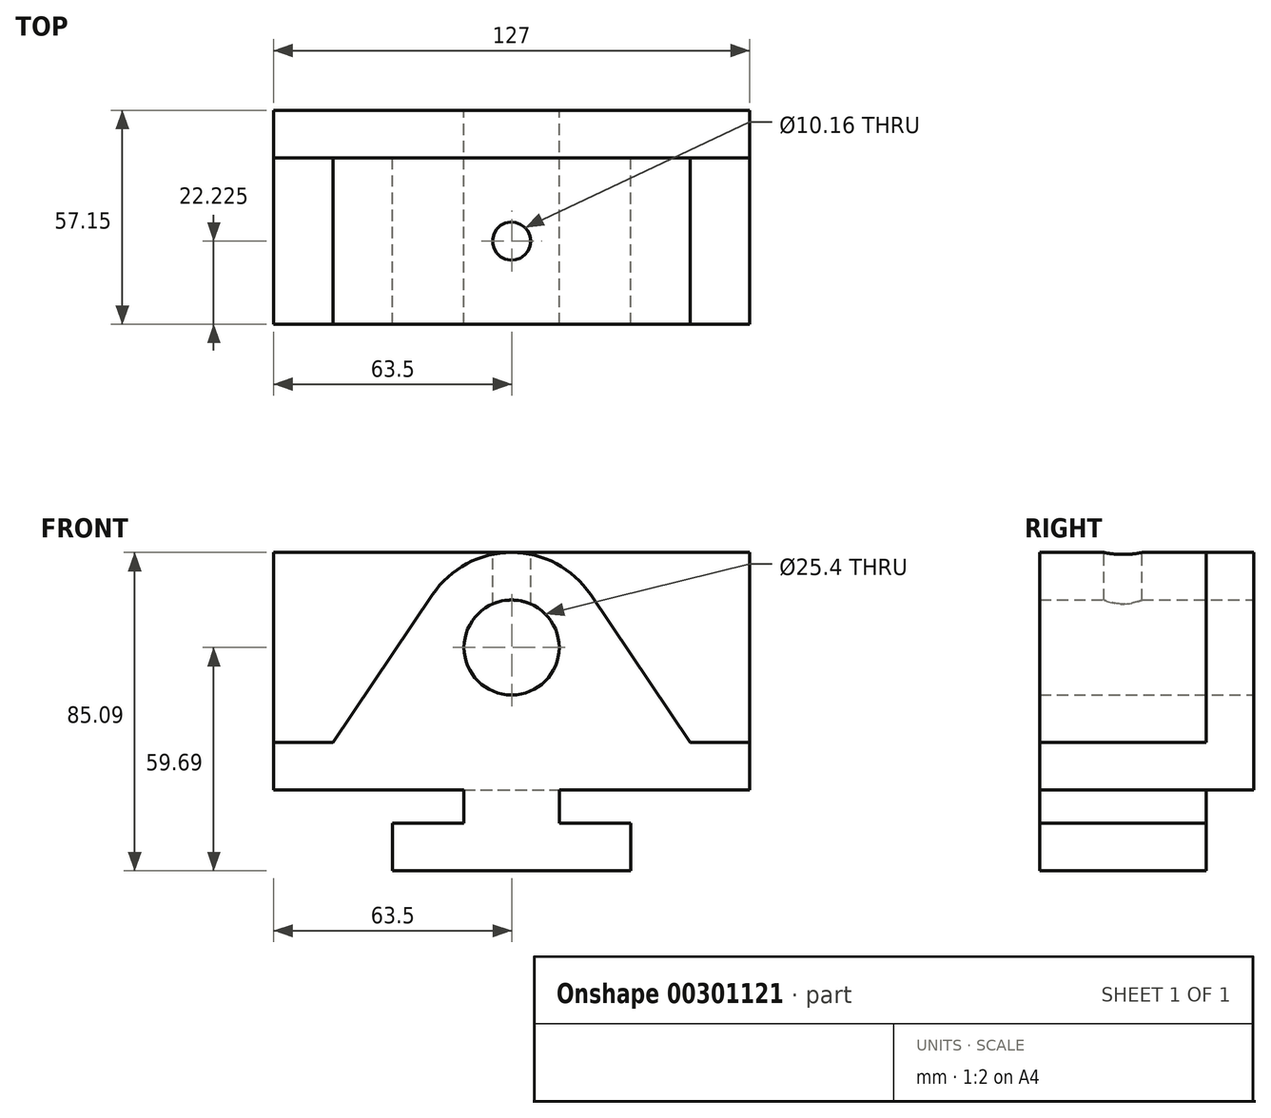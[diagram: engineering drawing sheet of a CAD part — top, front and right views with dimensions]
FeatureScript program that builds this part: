
annotation { "Feature Type Name" : "Feature", "Feature Type Description" : "" }
export const myFeature = defineFeature(function(context is Context, id is Id, definition is map)
    precondition{}
    {
        {
            var Q0;
            Q0=qCreatedBy(makeId("Front.planeOp"),FACE);
            var sketch = newSketch(context, id + "F0", { "sketchPlane" : qUnion([Q0])});
            skLineSegment(sketch, "E0", {"start": v(0, 0) * mm, "end": v(0, 12.7) * mm});
            skLineSegment(sketch, "E1", {"start": v(0, 12.7) * mm, "end": v(15.87, 12.7) * mm});
            skLineSegment(sketch, "E2", {"start": v(15.87, 12.7) * mm, "end": v(42.4, 52.25) * mm});
            skArc(sketch, "E3", {"start": v(84.6, 52.25) * mm, "mid": v(63.5, 63.5) * mm, "end": v(42.4, 52.25) * mm});
            skLineSegment(sketch, "E4", {"start": v(84.6, 52.25) * mm, "end": v(111.12, 12.7) * mm});
            skLineSegment(sketch, "E5", {"start": v(111.12, 12.7) * mm, "end": v(127, 12.7) * mm});
            skLineSegment(sketch, "E6", {"start": v(127, 12.7) * mm, "end": v(127, 0) * mm});
            skLineSegment(sketch, "E7", {"start": v(127, 0) * mm, "end": v(76.2, 0) * mm});
            skLineSegment(sketch, "E8", {"start": v(76.2, 0) * mm, "end": v(76.2, -8.89) * mm});
            skLineSegment(sketch, "E9", {"start": v(76.2, -8.89) * mm, "end": v(95.25, -8.89) * mm});
            skLineSegment(sketch, "E10", {"start": v(95.25, -8.89) * mm, "end": v(95.25, -21.6) * mm});
            skLineSegment(sketch, "E11", {"start": v(95.25, -21.6) * mm, "end": v(31.75, -21.6) * mm});
            skLineSegment(sketch, "E12", {"start": v(31.75, -21.6) * mm, "end": v(31.75, -8.89) * mm});
            skLineSegment(sketch, "E13", {"start": v(31.75, -8.89) * mm, "end": v(50.8, -8.89) * mm});
            skLineSegment(sketch, "E14", {"start": v(50.8, -8.89) * mm, "end": v(50.8, 0) * mm});
            skLineSegment(sketch, "E15", {"start": v(50.8, 0) * mm, "end": v(0, 0) * mm});
            skCircle(sketch, "E16", {"center": v(63.5, 38.1) * mm, "radius": 12.7 * mm});
            skPoint(sketch, "E17", {"position": v(63.5, 63.5) * mm});
            skSolve(sketch);
        }
        {
            var Q0;
            Q0 = qSketchRegion(id + "F0", true);
            extrude(context, id + "F1", {"entities" : qUnion([Q0]), "depth" : 44.45 * mm});
        }
        {
            var Q0;
            Q0=makeQuery(id+"F1.opExtrude","CAP_FACE",FACE,{"disambiguationData":[OSD([sQuery(id+"F0.wireOp",EDGE,"E0"),sQuery(id+"F0.wireOp",EDGE,"E1"),sQuery(id+"F0.wireOp",EDGE,"E2"),sQuery(id+"F0.wireOp",EDGE,"E3"),sQuery(id+"F0.wireOp",EDGE,"E4"),sQuery(id+"F0.wireOp",EDGE,"E5"),sQuery(id+"F0.wireOp",EDGE,"E6"),sQuery(id+"F0.wireOp",EDGE,"E7"),sQuery(id+"F0.wireOp",EDGE,"E8"),sQuery(id+"F0.wireOp",EDGE,"E9"),sQuery(id+"F0.wireOp",EDGE,"E10"),sQuery(id+"F0.wireOp",EDGE,"E11"),sQuery(id+"F0.wireOp",EDGE,"E12"),sQuery(id+"F0.wireOp",EDGE,"E13"),sQuery(id+"F0.wireOp",EDGE,"E14"),sQuery(id+"F0.wireOp",EDGE,"E15"),sQuery(id+"F0.wireOp",EDGE,"E16")])],"isStart":true});
            var sketch = newSketch(context, id + "F2", { "sketchPlane" : qUnion([Q0])});
            skLineSegment(sketch, "E18.bottom", {"start": v(0, 0) * mm, "end": v(-127, 0) * mm});
            skLineSegment(sketch, "E18.top", {"start": v(0, 63.5) * mm, "end": v(-127, 63.5) * mm});
            skLineSegment(sketch, "E18.left", {"start": v(0, 0) * mm, "end": v(0, 63.5) * mm});
            skLineSegment(sketch, "E18.right", {"start": v(-127, 0) * mm, "end": v(-127, 63.5) * mm});
            skSolve(sketch);
        }
        {
            var Q0;
            Q0 = qSketchRegion(id + "F2", true);
            extrude(context, id + "F3", {"entities" : qUnion([Q0]), "operationType" : NewBodyOperationType.ADD, "depth" : 12.7 * mm});
        }
        {
            var Q0;
            Q0=makeQuery(id+"F3.boolean.opBoolean","SPLIT",FACE,{"disambiguationData":[TD([makeQuery(id+"F1.opExtrude","SWEPT_FACE",FACE,{"disambiguationData":[OSD([sQuery(id+"F0.wireOp",EDGE,"E16")])]})])],"derivedFrom":makeQuery(id+"F3.opExtrude","CAP_FACE",FACE,{"disambiguationData":[OSD([sQuery(id+"F2.wireOp",EDGE,"E18.bottom"),sQuery(id+"F2.wireOp",EDGE,"E18.top"),sQuery(id+"F2.wireOp",EDGE,"E18.left"),sQuery(id+"F2.wireOp",EDGE,"E18.right")])],"isStart":true})});
            var sketch = newSketch(context, id + "F4", { "sketchPlane" : qUnion([Q0])});
            skSolve(sketch);
        }
        {
            var Q0;
            Q0 = qSketchRegion(id + "F4", true);
            var Q1;
            Q1=makeQuery(id+"F4.imprint","IMPRINT",FACE,{"disambiguationData":[TD([[makeQuery(id+"F4.imprint","IMPRINT",EDGE,{"derivedFrom":makeQuery(id+"F1.opExtrude","CAP_EDGE",EDGE,{"disambiguationData":[OSD([sQuery(id+"F0.wireOp",EDGE,"E16")])],"isStart":true})}),1.0]])]});
            extrude(context, id + "F5", {"entities" : qUnion([Q0, Q1]), "operationType" : NewBodyOperationType.REMOVE, "endBound" : BoundingType.THROUGH_ALL, "oppositeDirection" : true, "depth" : 25.4 * mm});
        }
        {
            var Q0;
            Q0=makeQuery(id+"F3.opExtrude","SWEPT_FACE",FACE,{"disambiguationData":[OSD([sQuery(id+"F2.wireOp",EDGE,"E18.top")])]});
            var sketch = newSketch(context, id + "F6", { "sketchPlane" : qUnion([Q0])});
            skPoint(sketch, "E19", {"position": v(63.5, -22.22) * mm});
            skCircle(sketch, "E20", {"center": v(63.5, -22.22) * mm, "radius": 5.08 * mm});
            skLineSegment(sketch, "E21", {"start": v(63.5, -22.22) * mm, "end": v(0, -22.23) * mm});
            skLineSegment(sketch, "E22", {"start": v(63.5, -22.23) * mm, "end": v(127, -22.23) * mm});
            skSolve(sketch);
        }
        {
            var Q0;
            {var subQ0=sQuery(id+"F6.wireOp",EDGE,"E21");var subQ1=sQuery(id+"F6.wireOp",EDGE,"E20");var subQ2=makeQuery(id+"F6.imprint","INTERSECT",VERTEX,{"derivedFrom":[subQ1,subQ0]});Q0=makeQuery(id+"F6.imprint","IMPRINT",FACE,{"disambiguationData":[TD([[makeQuery(id+"F6.imprint","IMPRINT",EDGE,{"disambiguationData":[TD([[subQ2,-1.0]])],"derivedFrom":subQ1}),1.0]])]});}
            var Q1;
            {var subQ0=sQuery(id+"F6.wireOp",EDGE,"E21");var subQ1=sQuery(id+"F6.wireOp",EDGE,"E20");var subQ2=makeQuery(id+"F6.imprint","INTERSECT",VERTEX,{"derivedFrom":[subQ1,subQ0]});Q1=makeQuery(id+"F6.imprint","IMPRINT",FACE,{"disambiguationData":[TD([[makeQuery(id+"F6.imprint","IMPRINT",EDGE,{"disambiguationData":[TD([[subQ2,1.0]])],"derivedFrom":subQ1}),1.0]])]});}
            extrude(context, id + "F7", {"entities" : qUnion([Q0, Q1]), "operationType" : NewBodyOperationType.REMOVE, "oppositeDirection" : true, "depth" : 25.4 * mm});
        }
    });
